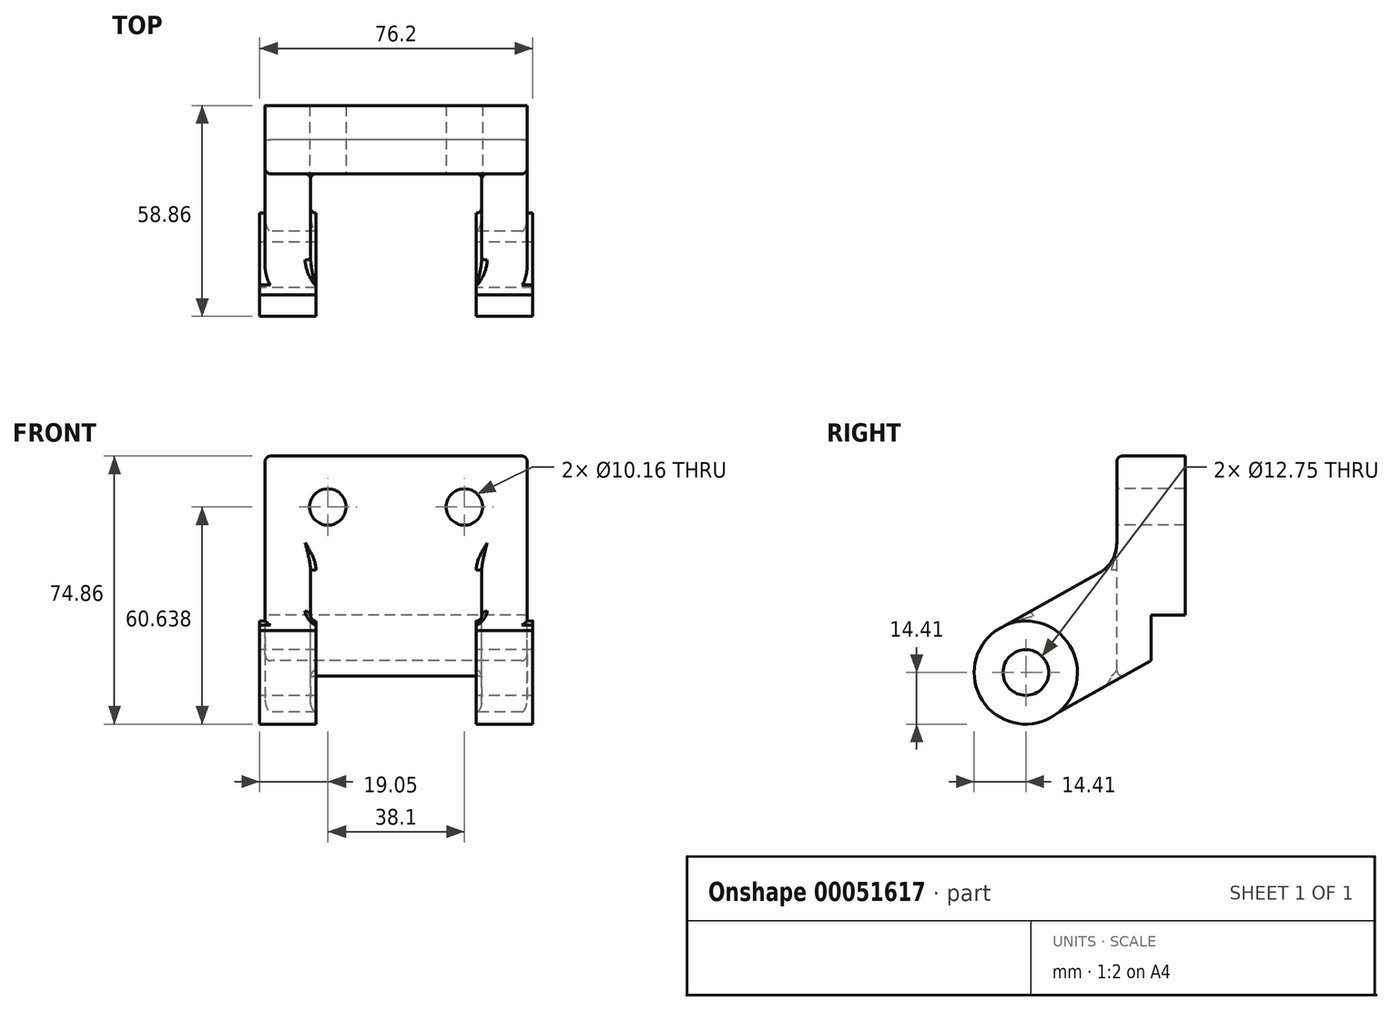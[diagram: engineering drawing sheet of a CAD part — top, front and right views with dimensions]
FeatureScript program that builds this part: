
annotation { "Feature Type Name" : "Feature", "Feature Type Description" : "" }
export const myFeature = defineFeature(function(context is Context, id is Id, definition is map)
    precondition{}
    {
        {
            var Q0;
            Q0=qCreatedBy(makeId("Right.planeOp"),FACE);
            var sketch = newSketch(context, id + "F0", { "sketchPlane" : qUnion([Q0])});
            skArc(sketch, "E0", {"start": v(5.47, -13.13) * mm, "mid": v(6.93, -12.42) * mm, "end": v(8.3, -11.55) * mm});
            skLineSegment(sketch, "E1.bottom", {"start": v(25.4, 60.45) * mm, "end": v(44.45, 60.45) * mm});
            skLineSegment(sketch, "E1.top", {"start": v(34.92, 16) * mm, "end": v(44.45, 16) * mm});
            skLineSegment(sketch, "E1.left", {"start": v(25.4, 60.45) * mm, "end": v(25.4, 30.56) * mm});
            skLineSegment(sketch, "E1.right", {"start": v(44.45, 60.45) * mm, "end": v(44.45, 16) * mm});
            skPoint(sketch, "E2", {"position": v(34.93, 3.3) * mm});
            skLineSegment(sketch, "E3", {"start": v(34.93, 3.3) * mm, "end": v(5.47, -13.13) * mm});
            skLineSegment(sketch, "E4.0", {"start": v(25.4, 30.56) * mm, "end": v(-8.39, 11.71) * mm});
            skLineSegment(sketch, "E5", {"start": v(34.93, 3.3) * mm, "end": v(34.92, 16) * mm});
            skPoint(sketch, "E6.orphan", {"position": v(25.4, 16) * mm});
            skArc(sketch, "E7", {"start": v(-5.56, 13.29) * mm, "mid": v(-12.28, -7.54) * mm, "end": v(9.33, -10.98) * mm});
            skSolve(sketch);
        }
        {
            var Q0;
            {var subQ4=sQuery(id+"F0.wireOp",EDGE,"E0");Q0=makeQuery(id+"F0.imprint","IMPRINT",FACE,{"disambiguationData":[TD([[makeQuery(id+"F0.imprint","IMPRINT",EDGE,{"derivedFrom":subQ4}),-1.0]])]});}
            extrude(context, id + "F1", {"entities" : qUnion([Q0]), "endBound" : BoundingType.SYMMETRIC, "depth" : 73.15 * mm});
        }
        {
            var Q0;
            Q0=makeQuery(id+"F1.opExtrude","SWEPT_FACE",FACE,{"disambiguationData":[OSD([sQuery(id+"F0.wireOp",EDGE,"E1.bottom")])]});
            var sketch = newSketch(context, id + "F2", { "sketchPlane" : qUnion([Q0])});
            skLineSegment(sketch, "E8.bottom", {"start": v(-23.88, -30.11) * mm, "end": v(23.88, -30.11) * mm});
            skLineSegment(sketch, "E8.top", {"start": v(-23.88, 25.4) * mm, "end": v(23.88, 25.4) * mm});
            skLineSegment(sketch, "E8.left", {"start": v(-23.88, -30.11) * mm, "end": v(-23.88, 25.4) * mm});
            skLineSegment(sketch, "E8.right", {"start": v(23.88, -30.11) * mm, "end": v(23.88, 25.4) * mm});
            skSolve(sketch);
        }
        {
            var Q0;
            Q0 = qSketchRegion(id + "F2", true);
            extrude(context, id + "F3", {"entities" : qUnion([Q0]), "operationType" : NewBodyOperationType.REMOVE, "endBound" : BoundingType.THROUGH_ALL, "oppositeDirection" : true, "depth" : 25.4 * mm});
        }
        {
            var Q0;
            Q0=makeQuery(id+"F1.opExtrude","CAP_FACE",FACE,{"disambiguationData":[OSD([sQuery(id+"F0.wireOp",EDGE,"E0"),sQuery(id+"F0.wireOp",EDGE,"E1.bottom"),sQuery(id+"F0.wireOp",EDGE,"E1.top"),sQuery(id+"F0.wireOp",EDGE,"E1.left"),sQuery(id+"F0.wireOp",EDGE,"E1.right"),sQuery(id+"F0.wireOp",EDGE,"E3"),sQuery(id+"F0.wireOp",EDGE,"E4.0"),sQuery(id+"F0.wireOp",EDGE,"E5"),sQuery(id+"F0.wireOp",EDGE,"E7")])],"isStart":false});
            var sketch = newSketch(context, id + "F4", { "sketchPlane" : qUnion([Q0])});
            skCircle(sketch, "E9", {"center": v(0, 0) * mm, "radius": 14.4 * mm});
            skSolve(sketch);
        }
        {
            var Q0;
            {var subQ0=sQuery(id+"F0.wireOp",EDGE,"E0");Q0=makeQuery(id+"F4.imprint","IMPRINT",FACE,{"disambiguationData":[TD([[makeQuery(id+"F4.imprint","IMPRINT",EDGE,{"derivedFrom":makeQuery(id+"F1.opExtrude","CAP_EDGE",EDGE,{"disambiguationData":[OSD([subQ0])],"isStart":false})}),1.0]])]});}
            var Q1;
            {var subQ0=sQuery(id+"F4.wireOp",EDGE,"E9");var subQ1=makeQuery(id+"F1.opExtrude","CAP_EDGE",EDGE,{"disambiguationData":[OSD([sQuery(id+"F0.wireOp",EDGE,"E4.0")])],"isStart":false});var subQ2=makeQuery(id+"F4.imprint","INTERSECT",VERTEX,{"disambiguationData":[OD(0.0)],"derivedFrom":[subQ1,subQ0]});Q1=makeQuery(id+"F4.imprint","IMPRINT",FACE,{"disambiguationData":[TD([[makeQuery(id+"F4.imprint","IMPRINT",EDGE,{"disambiguationData":[TD([[subQ2,1.0]])],"derivedFrom":subQ0}),1.0]])]});}
            var Q2;
            {var subQ1=sQuery(id+"F0.wireOp",EDGE,"E0");Q2=makeQuery(id+"F4.imprint","IMPRINT",FACE,{"disambiguationData":[TD([[makeQuery(id+"F4.imprint","IMPRINT",EDGE,{"derivedFrom":makeQuery(id+"F1.opExtrude","CAP_EDGE",EDGE,{"disambiguationData":[OSD([subQ1])],"isStart":false})}),-1.0]])]});}
            extrude(context, id + "F5", {"entities" : qUnion([Q0, Q1, Q2]), "operationType" : NewBodyOperationType.ADD, "depth" : 1.52 * mm});
        }
        {
            var Q0;
            Q0=makeQuery(id+"F5.opExtrude","CAP_FACE",FACE,{"disambiguationData":[OSD([sQuery(id+"F4.wireOp",EDGE,"E9")])],"isStart":false});
            extrude(context, id + "F6", {"entities" : qUnion([Q0]), "operationType" : NewBodyOperationType.ADD, "oppositeDirection" : true, "depth" : 15.75 * mm});
        }
        {
            var Q0;
            Q0=makeQuery(id+"F1.opExtrude","CAP_FACE",FACE,{"disambiguationData":[OSD([sQuery(id+"F0.wireOp",EDGE,"E0"),sQuery(id+"F0.wireOp",EDGE,"E1.bottom"),sQuery(id+"F0.wireOp",EDGE,"E1.top"),sQuery(id+"F0.wireOp",EDGE,"E1.left"),sQuery(id+"F0.wireOp",EDGE,"E1.right"),sQuery(id+"F0.wireOp",EDGE,"E3"),sQuery(id+"F0.wireOp",EDGE,"E4.0"),sQuery(id+"F0.wireOp",EDGE,"E5"),sQuery(id+"F0.wireOp",EDGE,"E7")])],"isStart":true});
            var sketch = newSketch(context, id + "F7", { "sketchPlane" : qUnion([Q0])});
            skCircle(sketch, "E10", {"center": v(0, 0) * mm, "radius": 14.4 * mm});
            skSolve(sketch);
        }
        {
            var Q0;
            {var subQ0=sQuery(id+"F0.wireOp",EDGE,"E0");Q0=makeQuery(id+"F7.imprint","IMPRINT",FACE,{"disambiguationData":[TD([[makeQuery(id+"F7.imprint","IMPRINT",EDGE,{"derivedFrom":makeQuery(id+"F1.opExtrude","CAP_EDGE",EDGE,{"disambiguationData":[OSD([subQ0])],"isStart":true})}),-1.0]])]});}
            var Q1;
            {var subQ0=sQuery(id+"F7.wireOp",EDGE,"E10");var subQ1=makeQuery(id+"F1.opExtrude","CAP_EDGE",EDGE,{"disambiguationData":[OSD([sQuery(id+"F0.wireOp",EDGE,"E4.0")])],"isStart":true});var subQ2=makeQuery(id+"F7.imprint","INTERSECT",VERTEX,{"disambiguationData":[OD(0.0)],"derivedFrom":[subQ1,subQ0]});var subQ3=makeQuery(id+"F7.imprint","INTERSECT",VERTEX,{"disambiguationData":[OD(1.0)],"derivedFrom":[subQ1,subQ0]});Q1=makeQuery(id+"F7.imprint","IMPRINT",FACE,{"disambiguationData":[TD([[makeQuery(id+"F7.imprint","IMPRINT",EDGE,{"disambiguationData":[TD([[subQ2,-1.0],[subQ3,1.0]])],"derivedFrom":subQ0}),1.0]])]});}
            var Q2;
            {var subQ1=sQuery(id+"F0.wireOp",EDGE,"E0");Q2=makeQuery(id+"F7.imprint","IMPRINT",FACE,{"disambiguationData":[TD([[makeQuery(id+"F7.imprint","IMPRINT",EDGE,{"derivedFrom":makeQuery(id+"F1.opExtrude","CAP_EDGE",EDGE,{"disambiguationData":[OSD([subQ1])],"isStart":true})}),1.0]])]});}
            extrude(context, id + "F8", {"entities" : qUnion([Q0, Q1, Q2]), "operationType" : NewBodyOperationType.ADD, "depth" : 1.52 * mm});
        }
        {
            var Q0;
            Q0=makeQuery(id+"F8.opExtrude","CAP_FACE",FACE,{"disambiguationData":[OSD([sQuery(id+"F7.wireOp",EDGE,"E10")])],"isStart":false});
            extrude(context, id + "F9", {"entities" : qUnion([Q0]), "operationType" : NewBodyOperationType.ADD, "oppositeDirection" : true, "depth" : 15.75 * mm});
        }
        {
            var Q0;
            Q0=makeQuery(id+"F8.opExtrude","CAP_FACE",FACE,{"disambiguationData":[OSD([sQuery(id+"F7.wireOp",EDGE,"E10")])],"isStart":false});
            var sketch = newSketch(context, id + "F10", { "sketchPlane" : qUnion([Q0])});
            skCircle(sketch, "E11", {"center": v(0, 0) * mm, "radius": 6.38 * mm});
            skSolve(sketch);
        }
        {
            var Q0;
            Q0=makeQuery(id+"F10.imprint","IMPRINT",FACE,{"disambiguationData":[TD([[makeQuery(id+"F10.imprint","IMPRINT",EDGE,{"derivedFrom":sQuery(id+"F10.wireOp",EDGE,"E11")}),1.0]])]});
            extrude(context, id + "F11", {"entities" : qUnion([Q0]), "operationType" : NewBodyOperationType.REMOVE, "endBound" : BoundingType.THROUGH_ALL, "oppositeDirection" : true, "depth" : 25.4 * mm});
        }
        {
            var Q0;
            Q0=makeQuery(id+"F3.boolean.opBoolean","MERGE",FACE,{"derivedFrom":[makeQuery(id+"F1.opExtrude","SWEPT_FACE",FACE,{"disambiguationData":[OSD([sQuery(id+"F0.wireOp",EDGE,"E1.left")])]}),makeQuery(id+"F3.opExtrude","SWEPT_FACE",FACE,{"disambiguationData":[OSD([sQuery(id+"F2.wireOp",EDGE,"E8.top")])]})]});
            var sketch = newSketch(context, id + "F12", { "sketchPlane" : qUnion([Q0])});
            skCircle(sketch, "E12", {"center": v(19.05, 46.23) * mm, "radius": 5.08 * mm});
            skCircle(sketch, "E13", {"center": v(-19.05, 46.23) * mm, "radius": 5.08 * mm});
            skSolve(sketch);
        }
        {
            var Q0;
            Q0 = qSketchRegion(id + "F12", true);
            extrude(context, id + "F13", {"entities" : qUnion([Q0]), "operationType" : NewBodyOperationType.REMOVE, "endBound" : BoundingType.THROUGH_ALL, "oppositeDirection" : true, "depth" : 25.4 * mm});
        }
        {
            var Q0;
            {var subQ0=sQuery(id+"F0.wireOp",EDGE,"E1.left");var subQ1=sQuery(id+"F0.wireOp",EDGE,"E4.0");Q0=makeQuery(id+"F3.boolean.opBoolean","SPLIT",EDGE,{"disambiguationData":[TD([makeQuery(id+"F3.opExtrude","SWEPT_FACE",FACE,{"disambiguationData":[OSD([sQuery(id+"F2.wireOp",EDGE,"E8.right")])]})])],"derivedFrom":makeQuery(id+"F1.opExtrude","SWEPT_EDGE",EDGE,{"disambiguationData":[OSD([subQ0,subQ1])]})});}
            var Q1;
            {var subQ0=sQuery(id+"F0.wireOp",EDGE,"E4.0");var subQ1=sQuery(id+"F0.wireOp",EDGE,"E1.left");Q1=makeQuery(id+"F3.boolean.opBoolean","SPLIT",EDGE,{"disambiguationData":[TD([makeQuery(id+"F3.opExtrude","SWEPT_FACE",FACE,{"disambiguationData":[OSD([sQuery(id+"F2.wireOp",EDGE,"E8.left")])]})])],"derivedFrom":makeQuery(id+"F1.opExtrude","SWEPT_EDGE",EDGE,{"disambiguationData":[OSD([subQ1,subQ0])]})});}
            fillet(context, id + "F14", {"entities" : qUnion([Q0, Q1]), "radius" : 9.65 * mm, "tangentPropagation" : true, "allowEdgeOverflow" : false});
        }
        {
            var Q0;
            {var subQ0=sQuery(id+"F0.wireOp",EDGE,"E7");var subQ1=sQuery(id+"F0.wireOp",EDGE,"E5");var subQ2=sQuery(id+"F0.wireOp",EDGE,"E3");var subQ3=sQuery(id+"F0.wireOp",EDGE,"E4.0");var subQ4=sQuery(id+"F4.wireOp",EDGE,"E9");Q0=makeQuery(id+"F5.boolean.opBoolean","SPLIT",EDGE,{"disambiguationData":[TD([makeQuery(id+"F1.opExtrude","CAP_FACE",FACE,{"disambiguationData":[OSD([sQuery(id+"F0.wireOp",EDGE,"E0"),sQuery(id+"F0.wireOp",EDGE,"E1.bottom"),sQuery(id+"F0.wireOp",EDGE,"E1.top"),sQuery(id+"F0.wireOp",EDGE,"E1.left"),sQuery(id+"F0.wireOp",EDGE,"E1.right"),subQ2,subQ3,subQ1,subQ0])],"isStart":false}),makeQuery(id+"F1.opExtrude","SWEPT_FACE",FACE,{"disambiguationData":[OSD([subQ2]),TDD([makeQuery(id+"F0.imprint","IMPRINT",EDGE,{"disambiguationData":[TD([[makeQuery(id+"F0.imprint","INTERSECT",VERTEX,{"derivedFrom":[subQ2,subQ1]}),-1.0]])],"derivedFrom":subQ2})])]}),makeQuery(id+"F1.opExtrude","SWEPT_FACE",FACE,{"disambiguationData":[OSD([subQ3])]}),makeQuery(id+"F1.opExtrude","SWEPT_FACE",FACE,{"disambiguationData":[OSD([subQ0])]}),makeQuery(id+"F5.opExtrude","SWEPT_FACE",FACE,{"disambiguationData":[OSD([subQ4])]}),makeQuery(id+"F5.opExtrude","CAP_FACE",FACE,{"disambiguationData":[OSD([subQ4])],"isStart":true})])],"derivedFrom":makeQuery(id+"F5.opExtrude","CAP_EDGE",EDGE,{"disambiguationData":[OSD([subQ4])],"isStart":true})});}
            var Q1;
            Q1=makeQuery(id+"F9.boolean.opBoolean","INTERSECT",EDGE,{"derivedFrom":[makeQuery(id+"F3.boolean.opBoolean","COPY",FACE,{"derivedFrom":makeQuery(id+"F3.opExtrude","SWEPT_FACE",FACE,{"disambiguationData":[OSD([sQuery(id+"F2.wireOp",EDGE,"E8.left")])]})}),makeQuery(id+"F9.opExtrude","SWEPT_FACE",FACE,{"disambiguationData":[OSD([sQuery(id+"F7.wireOp",EDGE,"E10")])]})]});
            var Q2;
            Q2=makeQuery(id+"F6.boolean.opBoolean","INTERSECT",EDGE,{"derivedFrom":[makeQuery(id+"F3.boolean.opBoolean","COPY",FACE,{"derivedFrom":makeQuery(id+"F3.opExtrude","SWEPT_FACE",FACE,{"disambiguationData":[OSD([sQuery(id+"F2.wireOp",EDGE,"E8.right")])]})}),makeQuery(id+"F6.opExtrude","SWEPT_FACE",FACE,{"disambiguationData":[OSD([sQuery(id+"F4.wireOp",EDGE,"E9")])]})]});
            var Q3;
            {var subQ0=sQuery(id+"F0.wireOp",EDGE,"E7");var subQ1=sQuery(id+"F0.wireOp",EDGE,"E4.0");var subQ2=sQuery(id+"F0.wireOp",EDGE,"E5");var subQ3=sQuery(id+"F0.wireOp",EDGE,"E3");var subQ4=sQuery(id+"F7.wireOp",EDGE,"E10");Q3=makeQuery(id+"F8.boolean.opBoolean","SPLIT",EDGE,{"disambiguationData":[TD([makeQuery(id+"F1.opExtrude","CAP_FACE",FACE,{"disambiguationData":[OSD([sQuery(id+"F0.wireOp",EDGE,"E0"),sQuery(id+"F0.wireOp",EDGE,"E1.bottom"),sQuery(id+"F0.wireOp",EDGE,"E1.top"),sQuery(id+"F0.wireOp",EDGE,"E1.left"),sQuery(id+"F0.wireOp",EDGE,"E1.right"),subQ3,subQ1,subQ2,subQ0])],"isStart":true}),makeQuery(id+"F1.opExtrude","SWEPT_FACE",FACE,{"disambiguationData":[OSD([subQ3]),TDD([makeQuery(id+"F0.imprint","IMPRINT",EDGE,{"disambiguationData":[TD([[makeQuery(id+"F0.imprint","INTERSECT",VERTEX,{"derivedFrom":[subQ3,subQ2]}),-1.0]])],"derivedFrom":subQ3})])]}),makeQuery(id+"F1.opExtrude","SWEPT_FACE",FACE,{"disambiguationData":[OSD([subQ1])]}),makeQuery(id+"F1.opExtrude","SWEPT_FACE",FACE,{"disambiguationData":[OSD([subQ0])]}),makeQuery(id+"F8.opExtrude","SWEPT_FACE",FACE,{"disambiguationData":[OSD([subQ4])]}),makeQuery(id+"F8.opExtrude","CAP_FACE",FACE,{"disambiguationData":[OSD([subQ4])],"isStart":true})])],"derivedFrom":makeQuery(id+"F8.opExtrude","CAP_EDGE",EDGE,{"disambiguationData":[OSD([subQ4])],"isStart":true})});}
            fillet(context, id + "F15", {"entities" : qUnion([Q0, Q1, Q2, Q3]), "radius" : 1.52 * mm, "tangentPropagation" : true, "allowEdgeOverflow" : false});
        }
        {
            var Q0;
            Q0=makeQuery(id+"F3.boolean.opBoolean","INTERSECT",EDGE,{"derivedFrom":[makeQuery(id+"F1.opExtrude","SWEPT_FACE",FACE,{"disambiguationData":[OSD([sQuery(id+"F0.wireOp",EDGE,"E4.0")])]}),makeQuery(id+"F3.opExtrude","SWEPT_FACE",FACE,{"disambiguationData":[OSD([sQuery(id+"F2.wireOp",EDGE,"E8.left")])]})]});
            var Q1;
            {var subQ0=makeQuery(id+"F3.opExtrude","SWEPT_FACE",FACE,{"disambiguationData":[OSD([sQuery(id+"F2.wireOp",EDGE,"E8.left")])]});var subQ1=sQuery(id+"F0.wireOp",EDGE,"E4.0");var subQ2=sQuery(id+"F0.wireOp",EDGE,"E1.left");Q1=makeQuery(id+"F14.opFillet","BLEND_EDGE",EDGE,{"blendedFrom":[makeQuery(id+"F3.boolean.opBoolean","SPLIT",EDGE,{"disambiguationData":[TD([subQ0])],"derivedFrom":makeQuery(id+"F1.opExtrude","SWEPT_EDGE",EDGE,{"disambiguationData":[OSD([subQ2,subQ1])]})}),makeQuery(id+"F3.boolean.opBoolean","COPY",FACE,{"derivedFrom":subQ0})],"blendedInto":[makeQuery(id+"F3.boolean.opBoolean","COPY",FACE,{"derivedFrom":subQ0})]});}
            var Q2;
            {var subQ0=sQuery(id+"F0.wireOp",EDGE,"E4.0");var subQ1=sQuery(id+"F0.wireOp",EDGE,"E1.left");var subQ2=makeQuery(id+"F1.opExtrude","CAP_FACE",FACE,{"disambiguationData":[OSD([sQuery(id+"F0.wireOp",EDGE,"E0"),sQuery(id+"F0.wireOp",EDGE,"E1.bottom"),sQuery(id+"F0.wireOp",EDGE,"E1.top"),subQ1,sQuery(id+"F0.wireOp",EDGE,"E1.right"),sQuery(id+"F0.wireOp",EDGE,"E3"),subQ0,sQuery(id+"F0.wireOp",EDGE,"E5"),sQuery(id+"F0.wireOp",EDGE,"E7")])],"isStart":true});Q2=makeQuery(id+"F14.opFillet","BLEND_EDGE",EDGE,{"blendedFrom":[makeQuery(id+"F3.boolean.opBoolean","SPLIT",EDGE,{"disambiguationData":[TD([makeQuery(id+"F3.opExtrude","SWEPT_FACE",FACE,{"disambiguationData":[OSD([sQuery(id+"F2.wireOp",EDGE,"E8.left")])]})])],"derivedFrom":makeQuery(id+"F1.opExtrude","SWEPT_EDGE",EDGE,{"disambiguationData":[OSD([subQ1,subQ0])]})}),subQ2],"blendedInto":[subQ2]});}
            var Q3;
            {var subQ0=sQuery(id+"F0.wireOp",EDGE,"E7");var subQ1=sQuery(id+"F0.wireOp",EDGE,"E4.0");var subQ2=sQuery(id+"F0.wireOp",EDGE,"E1.left");var subQ3=sQuery(id+"F7.wireOp",EDGE,"E10");Q3=makeQuery(id+"F8.boolean.opBoolean","SPLIT",EDGE,{"disambiguationData":[TD([makeQuery(id+"F1.opExtrude","CAP_FACE",FACE,{"disambiguationData":[OSD([sQuery(id+"F0.wireOp",EDGE,"E0"),sQuery(id+"F0.wireOp",EDGE,"E1.bottom"),sQuery(id+"F0.wireOp",EDGE,"E1.top"),subQ2,sQuery(id+"F0.wireOp",EDGE,"E1.right"),sQuery(id+"F0.wireOp",EDGE,"E3"),subQ1,sQuery(id+"F0.wireOp",EDGE,"E5"),subQ0])],"isStart":true}),makeQuery(id+"F1.opExtrude","SWEPT_FACE",FACE,{"disambiguationData":[OSD([subQ2])]}),makeQuery(id+"F1.opExtrude","SWEPT_FACE",FACE,{"disambiguationData":[OSD([subQ1])]}),makeQuery(id+"F1.opExtrude","SWEPT_FACE",FACE,{"disambiguationData":[OSD([subQ0])]}),makeQuery(id+"F3.opExtrude","SWEPT_FACE",FACE,{"disambiguationData":[OSD([sQuery(id+"F2.wireOp",EDGE,"E8.top")])]}),makeQuery(id+"F8.opExtrude","SWEPT_FACE",FACE,{"disambiguationData":[OSD([subQ3])]}),makeQuery(id+"F8.opExtrude","CAP_FACE",FACE,{"disambiguationData":[OSD([subQ3])],"isStart":true})])],"derivedFrom":makeQuery(id+"F1.opExtrude","CAP_EDGE",EDGE,{"disambiguationData":[OSD([subQ1])],"isStart":true})});}
            var Q4;
            Q4=makeQuery(id+"F3.boolean.opBoolean","INTERSECT",EDGE,{"derivedFrom":[makeQuery(id+"F1.opExtrude","SWEPT_FACE",FACE,{"disambiguationData":[OSD([sQuery(id+"F0.wireOp",EDGE,"E4.0")])]}),makeQuery(id+"F3.opExtrude","SWEPT_FACE",FACE,{"disambiguationData":[OSD([sQuery(id+"F2.wireOp",EDGE,"E8.right")])]})]});
            var Q5;
            {var subQ0=sQuery(id+"F0.wireOp",EDGE,"E7");var subQ1=sQuery(id+"F0.wireOp",EDGE,"E1.left");var subQ2=sQuery(id+"F0.wireOp",EDGE,"E4.0");var subQ3=sQuery(id+"F4.wireOp",EDGE,"E9");Q5=makeQuery(id+"F5.boolean.opBoolean","SPLIT",EDGE,{"disambiguationData":[TD([makeQuery(id+"F1.opExtrude","CAP_FACE",FACE,{"disambiguationData":[OSD([sQuery(id+"F0.wireOp",EDGE,"E0"),sQuery(id+"F0.wireOp",EDGE,"E1.bottom"),sQuery(id+"F0.wireOp",EDGE,"E1.top"),subQ1,sQuery(id+"F0.wireOp",EDGE,"E1.right"),sQuery(id+"F0.wireOp",EDGE,"E3"),subQ2,sQuery(id+"F0.wireOp",EDGE,"E5"),subQ0])],"isStart":false}),makeQuery(id+"F1.opExtrude","SWEPT_FACE",FACE,{"disambiguationData":[OSD([subQ1])]}),makeQuery(id+"F1.opExtrude","SWEPT_FACE",FACE,{"disambiguationData":[OSD([subQ2])]}),makeQuery(id+"F1.opExtrude","SWEPT_FACE",FACE,{"disambiguationData":[OSD([subQ0])]}),makeQuery(id+"F3.opExtrude","SWEPT_FACE",FACE,{"disambiguationData":[OSD([sQuery(id+"F2.wireOp",EDGE,"E8.top")])]}),makeQuery(id+"F5.opExtrude","SWEPT_FACE",FACE,{"disambiguationData":[OSD([subQ3])]}),makeQuery(id+"F5.opExtrude","CAP_FACE",FACE,{"disambiguationData":[OSD([subQ3])],"isStart":true})])],"derivedFrom":makeQuery(id+"F1.opExtrude","CAP_EDGE",EDGE,{"disambiguationData":[OSD([subQ2])],"isStart":false})});}
            var Q6;
            {var subQ0=sQuery(id+"F0.wireOp",EDGE,"E4.0");var subQ1=sQuery(id+"F0.wireOp",EDGE,"E1.left");var subQ2=makeQuery(id+"F1.opExtrude","CAP_FACE",FACE,{"disambiguationData":[OSD([sQuery(id+"F0.wireOp",EDGE,"E0"),sQuery(id+"F0.wireOp",EDGE,"E1.bottom"),sQuery(id+"F0.wireOp",EDGE,"E1.top"),subQ1,sQuery(id+"F0.wireOp",EDGE,"E1.right"),sQuery(id+"F0.wireOp",EDGE,"E3"),subQ0,sQuery(id+"F0.wireOp",EDGE,"E5"),sQuery(id+"F0.wireOp",EDGE,"E7")])],"isStart":false});Q6=makeQuery(id+"F14.opFillet","BLEND_EDGE",EDGE,{"blendedFrom":[makeQuery(id+"F3.boolean.opBoolean","SPLIT",EDGE,{"disambiguationData":[TD([makeQuery(id+"F3.opExtrude","SWEPT_FACE",FACE,{"disambiguationData":[OSD([sQuery(id+"F2.wireOp",EDGE,"E8.right")])]})])],"derivedFrom":makeQuery(id+"F1.opExtrude","SWEPT_EDGE",EDGE,{"disambiguationData":[OSD([subQ1,subQ0])]})}),subQ2],"blendedInto":[subQ2]});}
            var Q7;
            {var subQ0=makeQuery(id+"F3.opExtrude","SWEPT_FACE",FACE,{"disambiguationData":[OSD([sQuery(id+"F2.wireOp",EDGE,"E8.right")])]});var subQ1=sQuery(id+"F0.wireOp",EDGE,"E1.left");var subQ2=sQuery(id+"F0.wireOp",EDGE,"E4.0");Q7=makeQuery(id+"F14.opFillet","BLEND_EDGE",EDGE,{"blendedFrom":[makeQuery(id+"F3.boolean.opBoolean","SPLIT",EDGE,{"disambiguationData":[TD([subQ0])],"derivedFrom":makeQuery(id+"F1.opExtrude","SWEPT_EDGE",EDGE,{"disambiguationData":[OSD([subQ1,subQ2])]})}),makeQuery(id+"F3.boolean.opBoolean","COPY",FACE,{"derivedFrom":subQ0})],"blendedInto":[makeQuery(id+"F3.boolean.opBoolean","COPY",FACE,{"derivedFrom":subQ0})]});}
            var Q8;
            Q8=makeQuery(id+"F1.opExtrude","SWEPT_EDGE",EDGE,{"disambiguationData":[OSD([sQuery(id+"F0.wireOp",EDGE,"E1.bottom"),sQuery(id+"F0.wireOp",EDGE,"E1.left")])]});
            var Q9;
            {var subQ0=sQuery(id+"F0.wireOp",EDGE,"E3");Q9=makeQuery(id+"F3.boolean.opBoolean","INTERSECT",EDGE,{"derivedFrom":[makeQuery(id+"F1.opExtrude","SWEPT_FACE",FACE,{"disambiguationData":[OSD([subQ0]),TDD([makeQuery(id+"F0.imprint","IMPRINT",EDGE,{"disambiguationData":[TD([[makeQuery(id+"F0.imprint","INTERSECT",VERTEX,{"derivedFrom":[subQ0,sQuery(id+"F0.wireOp",EDGE,"E5")]}),-1.0]])],"derivedFrom":subQ0})])]}),makeQuery(id+"F3.opExtrude","SWEPT_FACE",FACE,{"disambiguationData":[OSD([sQuery(id+"F2.wireOp",EDGE,"E8.top")])]})]});}
            var Q10;
            Q10=makeQuery(id+"F3.boolean.opBoolean","COPY",EDGE,{"derivedFrom":makeQuery(id+"F3.opExtrude","SWEPT_EDGE",EDGE,{"disambiguationData":[OSD([sQuery(id+"F0.wireOp",EDGE,"E1.bottom"),sQuery(id+"F0.wireOp",EDGE,"E1.left"),sQuery(id+"F2.wireOp",EDGE,"E8.top"),sQuery(id+"F2.wireOp",EDGE,"E8.left")])]})});
            var Q11;
            Q11=makeQuery(id+"F1.opExtrude","CAP_EDGE",EDGE,{"disambiguationData":[OSD([sQuery(id+"F0.wireOp",EDGE,"E1.left")])],"isStart":false});
            var Q12;
            Q12=makeQuery(id+"F3.boolean.opBoolean","COPY",EDGE,{"derivedFrom":makeQuery(id+"F3.opExtrude","SWEPT_EDGE",EDGE,{"disambiguationData":[OSD([sQuery(id+"F0.wireOp",EDGE,"E1.bottom"),sQuery(id+"F0.wireOp",EDGE,"E1.left"),sQuery(id+"F2.wireOp",EDGE,"E8.top"),sQuery(id+"F2.wireOp",EDGE,"E8.right")])]})});
            fillet(context, id + "F16", {"entities" : qUnion([Q0, Q1, Q2, Q3, Q4, Q5, Q6, Q7, Q8, Q9, Q10, Q11, Q12]), "radius" : 1.52 * mm, "tangentPropagation" : true, "allowEdgeOverflow" : false});
        }
        {
            var Q0;
            {var subQ0=sQuery(id+"F0.wireOp",EDGE,"E3");Q0=makeQuery(id+"F1.opExtrude","CAP_EDGE",EDGE,{"disambiguationData":[OSD([subQ0]),TDD([makeQuery(id+"F0.imprint","IMPRINT",EDGE,{"disambiguationData":[TD([[makeQuery(id+"F0.imprint","INTERSECT",VERTEX,{"derivedFrom":[subQ0,sQuery(id+"F0.wireOp",EDGE,"E5")]}),-1.0]])],"derivedFrom":subQ0})])],"isStart":true});}
            var Q1;
            {var subQ0=sQuery(id+"F0.wireOp",EDGE,"E3");Q1=makeQuery(id+"F1.opExtrude","CAP_EDGE",EDGE,{"disambiguationData":[OSD([subQ0]),TDD([makeQuery(id+"F0.imprint","IMPRINT",EDGE,{"disambiguationData":[TD([[makeQuery(id+"F0.imprint","INTERSECT",VERTEX,{"derivedFrom":[subQ0,sQuery(id+"F0.wireOp",EDGE,"E5")]}),-1.0]])],"derivedFrom":subQ0})])],"isStart":false});}
            var Q2;
            Q2=makeQuery(id+"F1.opExtrude","CAP_EDGE",EDGE,{"disambiguationData":[OSD([sQuery(id+"F0.wireOp",EDGE,"E1.bottom")])],"isStart":true});
            var Q3;
            Q3=makeQuery(id+"F1.opExtrude","CAP_EDGE",EDGE,{"disambiguationData":[OSD([sQuery(id+"F0.wireOp",EDGE,"E1.bottom")])],"isStart":false});
            fillet(context, id + "F17", {"entities" : qUnion([Q0, Q1, Q2, Q3]), "radius" : 1.52 * mm, "tangentPropagation" : true, "allowEdgeOverflow" : false});
        }
    });
